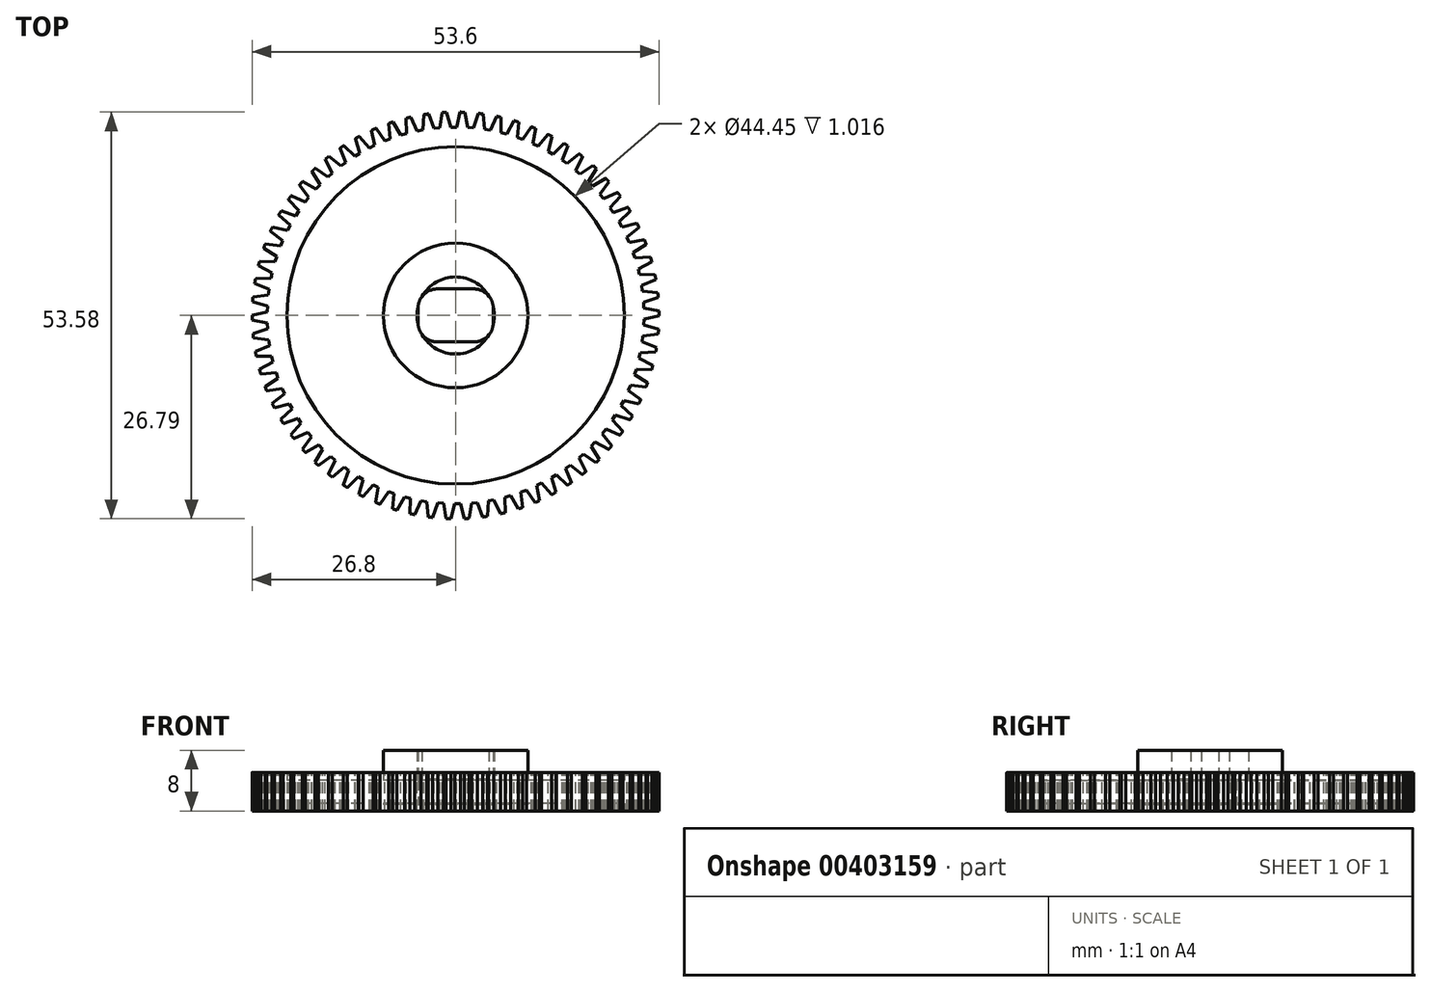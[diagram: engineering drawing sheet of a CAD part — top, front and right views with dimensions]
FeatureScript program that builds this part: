
annotation { "Feature Type Name" : "Feature", "Feature Type Description" : "" }
export const myFeature = defineFeature(function(context is Context, id is Id, definition is map)
    precondition{}
    {
        {
            var Q0;
            Q0=qCreatedBy(makeId("Top.planeOp"),FACE);
            var sketch = newSketch(context, id + "F0", { "sketchPlane" : qUnion([Q0])});
            skCircle(sketch, "E0", {"center": v(0, 0) * mm, "radius": 26.8 * mm});
            skCircle(sketch, "E1", {"center": v(0, 0) * mm, "radius": 22.23 * mm});
            skCircle(sketch, "E2", {"center": v(0, 0) * mm, "radius": 9.53 * mm});
            skLineSegment(sketch, "E3.bottom", {"start": v(2.41, -3.5) * mm, "end": v(-2.41, -3.5) * mm});
            skLineSegment(sketch, "E3.top", {"start": v(2.41, 3.5) * mm, "end": v(-2.41, 3.5) * mm});
            skLineSegment(sketch, "E3.left", {"start": v(4.95, -0.95) * mm, "end": v(4.95, 0.95) * mm});
            skLineSegment(sketch, "E3.right", {"start": v(-4.95, -0.95) * mm, "end": v(-4.95, 0.95) * mm});
            skPoint(sketch, "E4.visualSharp", {"position": v(-4.95, -3.5) * mm});
            skArc(sketch, "E4.filletArc", {"start": v(-4.95, -0.95) * mm, "mid": v(-4.2, -2.75) * mm, "end": v(-2.41, -3.5) * mm});
            skPoint(sketch, "E5.visualSharp", {"position": v(4.95, -3.5) * mm});
            skArc(sketch, "E5.filletArc", {"start": v(2.41, -3.5) * mm, "mid": v(4.2, -2.75) * mm, "end": v(4.95, -0.95) * mm});
            skPoint(sketch, "E6.visualSharp", {"position": v(4.95, 3.5) * mm});
            skArc(sketch, "E6.filletArc", {"start": v(4.95, 0.95) * mm, "mid": v(4.2, 2.75) * mm, "end": v(2.41, 3.5) * mm});
            skPoint(sketch, "E7.visualSharp", {"position": v(-4.95, 3.5) * mm});
            skArc(sketch, "E7.filletArc", {"start": v(-2.41, 3.5) * mm, "mid": v(-4.2, 2.75) * mm, "end": v(-4.95, 0.95) * mm});
            skSolve(sketch);
        }
        {
            var Q0;
            Q0=makeQuery(id+"F0.imprint","IMPRINT",FACE,{"disambiguationData":[TD([[makeQuery(id+"F0.imprint","IMPRINT",EDGE,{"derivedFrom":sQuery(id+"F0.wireOp",EDGE,"E0")}),1.0]])]});
            extrude(context, id + "F1", {"entities" : qUnion([Q0]), "endBound" : BoundingType.SYMMETRIC, "depth" : 5.08 * mm});
        }
        {
            var Q0;
            Q0=makeQuery(id+"F0.imprint","IMPRINT",FACE,{"disambiguationData":[TD([[makeQuery(id+"F0.imprint","IMPRINT",EDGE,{"derivedFrom":sQuery(id+"F0.wireOp",EDGE,"E1")}),1.0]])]});
            extrude(context, id + "F2", {"entities" : qUnion([Q0]), "operationType" : NewBodyOperationType.ADD, "endBound" : BoundingType.SYMMETRIC, "depth" : 3.05 * mm});
        }
        {
            var Q0;
            Q0=makeQuery(id+"F0.imprint","IMPRINT",FACE,{"disambiguationData":[TD([[makeQuery(id+"F0.imprint","IMPRINT",EDGE,{"derivedFrom":sQuery(id+"F0.wireOp",EDGE,"E2")}),1.0]])]});
            extrude(context, id + "F3", {"entities" : qUnion([Q0]), "operationType" : NewBodyOperationType.ADD, "endBound" : BoundingType.SYMMETRIC, "depth" : 3.3 * mm});
        }
        {
            var Q0;
            Q0=makeQuery(id+"F3.opExtrude","CAP_FACE",FACE,{"disambiguationData":[OSD([sQuery(id+"F0.wireOp",EDGE,"E2"),sQuery(id+"F0.wireOp",EDGE,"E3.bottom"),sQuery(id+"F0.wireOp",EDGE,"E3.top"),sQuery(id+"F0.wireOp",EDGE,"E3.left"),sQuery(id+"F0.wireOp",EDGE,"E3.right")])],"isStart":false});
            var sketch = newSketch(context, id + "F4", { "sketchPlane" : qUnion([Q0])});
            skCircle(sketch, "E8", {"center": v(0, 0) * mm, "radius": 5.08 * mm});
            skCircle(sketch, "E9", {"center": v(0, 0) * mm, "radius": 9.53 * mm});
            skSolve(sketch);
        }
        {
            var Q0;
            Q0=makeQuery(id+"F4.imprint","IMPRINT",FACE,{"disambiguationData":[TD([[makeQuery(id+"F4.imprint","IMPRINT",EDGE,{"derivedFrom":sQuery(id+"F4.wireOp",EDGE,"E9")}),1.0]])]});
            var Q1;
            {var subQ0=sQuery(id+"F4.wireOp",EDGE,"E8");var subQ1=makeQuery(id+"F3.opExtrude","CAP_EDGE",EDGE,{"disambiguationData":[OSD([sQuery(id+"F0.wireOp",EDGE,"E3.bottom")])],"isStart":false});var subQ2=makeQuery(id+"F4.imprint","INTERSECT",VERTEX,{"disambiguationData":[OD(1.0)],"derivedFrom":[subQ1,subQ0]});Q1=makeQuery(id+"F4.imprint","IMPRINT",FACE,{"disambiguationData":[TD([[makeQuery(id+"F4.imprint","IMPRINT",EDGE,{"disambiguationData":[TD([[subQ2,-1.0]])],"derivedFrom":subQ0}),-1.0]])]});}
            var Q2;
            {var subQ0=sQuery(id+"F4.wireOp",EDGE,"E8");var subQ1=makeQuery(id+"F3.opExtrude","CAP_EDGE",EDGE,{"disambiguationData":[OSD([sQuery(id+"F0.wireOp",EDGE,"E3.right")])],"isStart":false});var subQ2=makeQuery(id+"F4.imprint","INTERSECT",VERTEX,{"disambiguationData":[OD(1.0)],"derivedFrom":[subQ1,subQ0]});Q2=makeQuery(id+"F4.imprint","IMPRINT",FACE,{"disambiguationData":[TD([[makeQuery(id+"F4.imprint","IMPRINT",EDGE,{"disambiguationData":[TD([[subQ2,-1.0]])],"derivedFrom":subQ0}),-1.0]])]});}
            var Q3;
            {var subQ0=sQuery(id+"F4.wireOp",EDGE,"E8");var subQ1=makeQuery(id+"F3.opExtrude","CAP_EDGE",EDGE,{"disambiguationData":[OSD([sQuery(id+"F0.wireOp",EDGE,"E3.top")])],"isStart":false});var subQ2=makeQuery(id+"F4.imprint","INTERSECT",VERTEX,{"disambiguationData":[OD(1.0)],"derivedFrom":[subQ1,subQ0]});Q3=makeQuery(id+"F4.imprint","IMPRINT",FACE,{"disambiguationData":[TD([[makeQuery(id+"F4.imprint","IMPRINT",EDGE,{"disambiguationData":[TD([[subQ2,-1.0]])],"derivedFrom":subQ0}),-1.0]])]});}
            var Q4;
            {var subQ0=sQuery(id+"F4.wireOp",EDGE,"E8");var subQ1=makeQuery(id+"F3.opExtrude","CAP_EDGE",EDGE,{"disambiguationData":[OSD([sQuery(id+"F0.wireOp",EDGE,"E3.top")])],"isStart":false});var subQ2=makeQuery(id+"F4.imprint","INTERSECT",VERTEX,{"disambiguationData":[OD(0.0)],"derivedFrom":[subQ1,subQ0]});Q4=makeQuery(id+"F4.imprint","IMPRINT",FACE,{"disambiguationData":[TD([[makeQuery(id+"F4.imprint","IMPRINT",EDGE,{"disambiguationData":[TD([[subQ2,1.0]])],"derivedFrom":subQ0}),-1.0]])]});}
            extrude(context, id + "F5", {"entities" : qUnion([Q0, Q1, Q2, Q3, Q4]), "operationType" : NewBodyOperationType.ADD, "depth" : 3.8 * mm});
        }
        {
            var Q0;
            Q0=makeQuery(id+"F1.opExtrude","CAP_FACE",FACE,{"disambiguationData":[OSD([sQuery(id+"F0.wireOp",EDGE,"E0"),sQuery(id+"F0.wireOp",EDGE,"E1")])],"isStart":false});
            var sketch = newSketch(context, id + "F6", { "sketchPlane" : qUnion([Q0])});
            skLineSegment(sketch, "E10", {"start": v(-3.56, 26.56) * mm, "end": v(-2.86, 24.65) * mm});
            skLineSegment(sketch, "E11", {"start": v(-2.86, 24.65) * mm, "end": v(-2.1, 24.73) * mm});
            skLineSegment(sketch, "E12", {"start": v(-2.1, 24.73) * mm, "end": v(-1.8, 26.74) * mm});
            skLineSegment(sketch, "E13", {"start": v(-1.8, 26.74) * mm, "end": v(-3.56, 26.56) * mm, "construction": true});
            skLineSegment(sketch, "E14", {"start": v(-3.56, 26.56) * mm, "end": v(-2.74, 27.3) * mm});
            skLineSegment(sketch, "E15", {"start": v(-1.8, 26.74) * mm, "end": v(-2.74, 27.3) * mm});
            skSolve(sketch);
        }
        {
            var Q0;
            Q0=qCreatedBy(makeId("Right.planeOp"),FACE);
            var sketch = newSketch(context, id + "F7", { "sketchPlane" : qUnion([Q0])});
            skLineSegment(sketch, "E16", {"start": v(0, 0) * mm, "end": v(0, 17.73) * mm});
            skSolve(sketch);
        }
        {
            var Q0;
            Q0=makeQuery(id+"F6.imprint","IMPRINT",FACE,{"disambiguationData":[TD([[makeQuery(id+"F6.imprint","IMPRINT",EDGE,{"derivedFrom":sQuery(id+"F6.wireOp",EDGE,"E10")}),1.0]])]});
            var Q1;
            {var subQ0=sQuery(id+"F6.wireOp",EDGE,"E14");Q1=makeQuery(id+"F6.imprint","IMPRINT",FACE,{"disambiguationData":[TD([[makeQuery(id+"F6.imprint","IMPRINT",EDGE,{"derivedFrom":subQ0}),-1.0]])]});}
            extrude(context, id + "F8", {"entities" : qUnion([Q0, Q1]), "operationType" : NewBodyOperationType.REMOVE, "endBound" : BoundingType.THROUGH_ALL, "oppositeDirection" : true, "depth" : 25.4 * mm});
        }
        {
            var Q0;
            Q0=makeQuery(id+"F8.boolean.opBoolean","COPY",FACE,{"derivedFrom":makeQuery(id+"F8.opExtrude","SWEPT_FACE",FACE,{"disambiguationData":[OSD([sQuery(id+"F6.wireOp",EDGE,"E10")])]})});
            var Q1;
            Q1=makeQuery(id+"F8.boolean.opBoolean","COPY",FACE,{"derivedFrom":makeQuery(id+"F8.opExtrude","SWEPT_FACE",FACE,{"disambiguationData":[OSD([sQuery(id+"F6.wireOp",EDGE,"E11")])]})});
            var Q2;
            Q2=makeQuery(id+"F8.boolean.opBoolean","COPY",FACE,{"derivedFrom":makeQuery(id+"F8.opExtrude","SWEPT_FACE",FACE,{"disambiguationData":[OSD([sQuery(id+"F6.wireOp",EDGE,"E12")])]})});
            var Q3;
            Q3=sQuery(id+"F7.wireOp",EDGE,"E16");
            circularPattern(context, id + "F9", {"patternType" : PatternType.FACE, "faces" : qUnion([Q0, Q1, Q2]), "axis" : qUnion([Q3]), "angle" : 360 * degree, "instanceCount" : 70, "equalSpace" : true});
        }
    });
